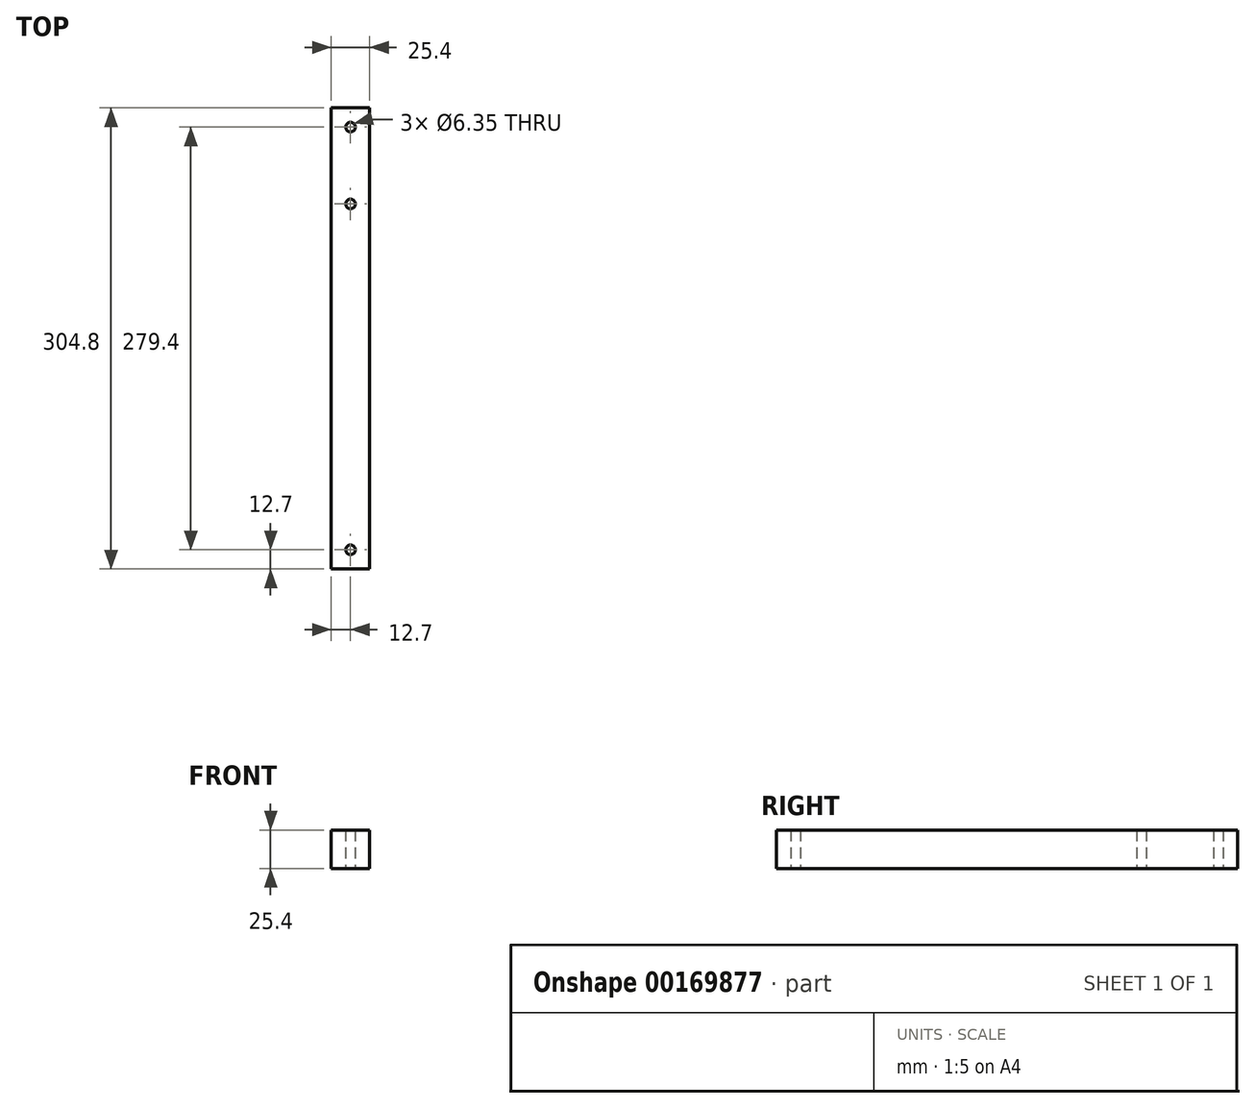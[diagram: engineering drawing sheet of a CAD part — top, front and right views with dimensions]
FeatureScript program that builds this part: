
annotation { "Feature Type Name" : "Feature", "Feature Type Description" : "" }
export const myFeature = defineFeature(function(context is Context, id is Id, definition is map)
    precondition{}
    {
        {
            var Q0;
            Q0=qCreatedBy(makeId("Top.planeOp"),FACE);
            var sketch = newSketch(context, id + "F0", { "sketchPlane" : qUnion([Q0])});
            skLineSegment(sketch, "E0.bottom", {"start": v(0, 0) * mm, "end": v(-25.4, 0) * mm});
            skLineSegment(sketch, "E0.top", {"start": v(0, -304.8) * mm, "end": v(-25.4, -304.8) * mm});
            skLineSegment(sketch, "E0.left", {"start": v(0, 0) * mm, "end": v(0, -304.8) * mm});
            skLineSegment(sketch, "E0.right", {"start": v(-25.4, 0) * mm, "end": v(-25.4, -304.8) * mm});
            skLineSegment(sketch, "E1", {"start": v(-12.7, 0) * mm, "end": v(-12.7, -304.8) * mm, "construction": true});
            skLineSegment(sketch, "E2", {"start": v(0, -152.4) * mm, "end": v(-12.7, -152.4) * mm, "construction": true});
            skCircle(sketch, "E3", {"center": v(-12.7, -12.7) * mm, "radius": 3.18 * mm});
            skCircle(sketch, "E4.MirrorC", {"center": v(-12.7, -292.1) * mm, "radius": 3.18 * mm});
            skCircle(sketch, "E5", {"center": v(-12.7, -63.5) * mm, "radius": 3.18 * mm});
            skSolve(sketch);
        }
        {
            var Q0;
            Q0 = qSketchRegion(id + "F0", true);
            extrude(context, id + "F1", {"entities" : qUnion([Q0]), "depth" : 25.4 * mm});
        }
    });
